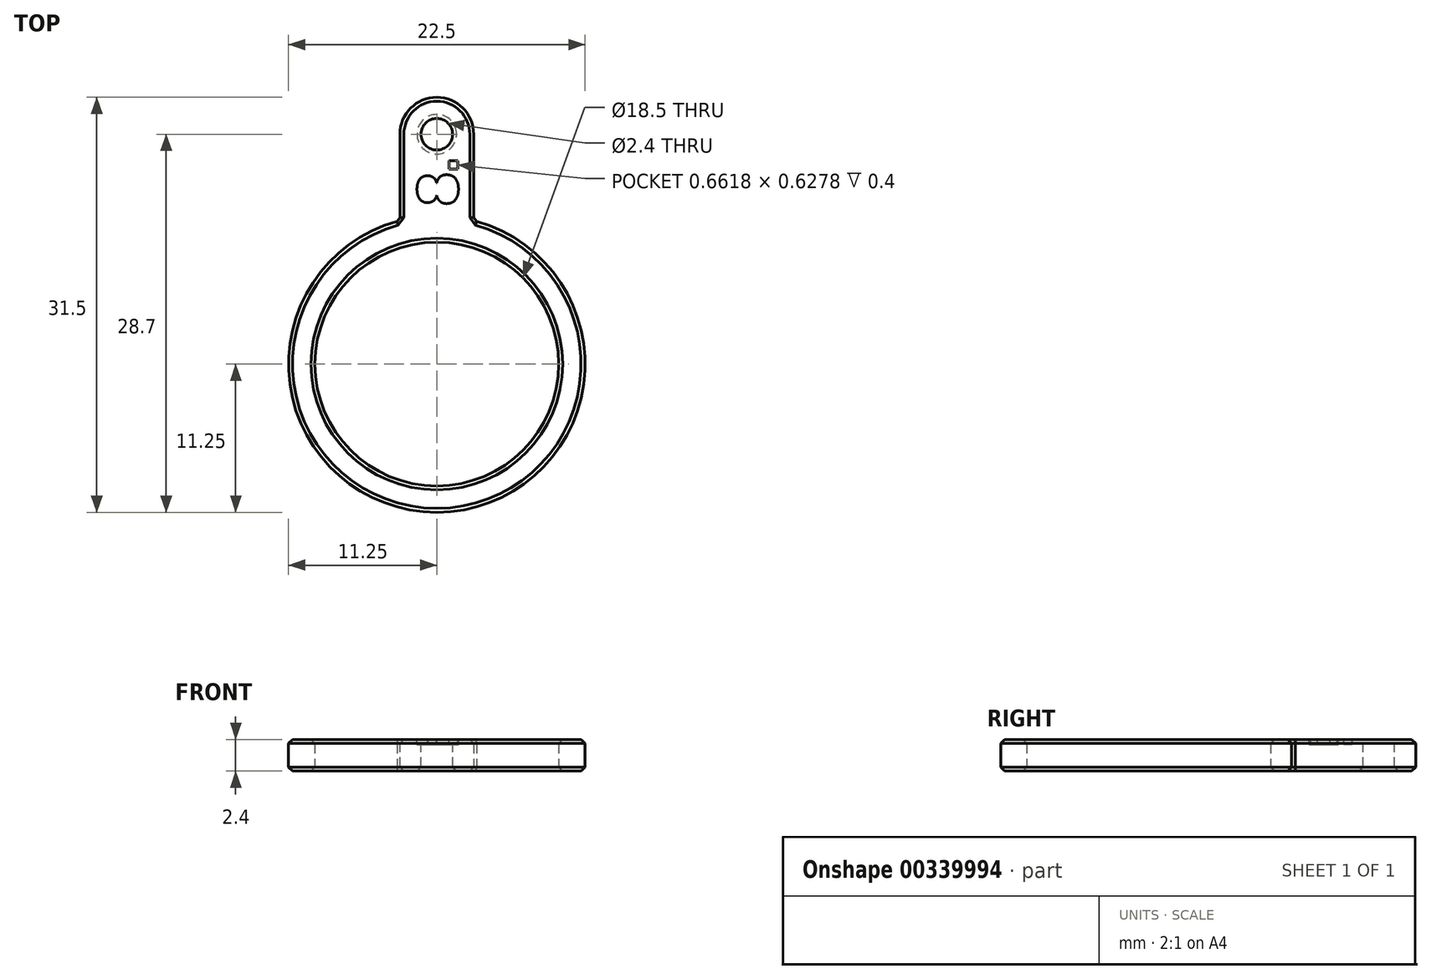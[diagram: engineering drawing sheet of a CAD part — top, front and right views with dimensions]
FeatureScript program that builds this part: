
annotation { "Feature Type Name" : "Feature", "Feature Type Description" : "" }
export const myFeature = defineFeature(function(context is Context, id is Id, definition is map)
    precondition{}
    {
        {
            var Q0;
            Q0=qCreatedBy(makeId("Top.planeOp"),FACE);
            var sketch = newSketch(context, id + "F0", { "sketchPlane" : qUnion([Q0])});
            skCircle(sketch, "E0", {"center": v(0, 0) * mm, "radius": 9.25 * mm});
            skCircle(sketch, "E1", {"center": v(0, 0) * mm, "radius": 11.25 * mm});
            skLineSegment(sketch, "E2.bottom", {"start": v(2.8, 2.25) * mm, "end": v(-2.8, 2.25) * mm});
            skLineSegment(sketch, "E2.top", {"start": v(2.8, 20.25) * mm, "end": v(-2.8, 20.25) * mm});
            skLineSegment(sketch, "E2.left", {"start": v(2.8, 2.25) * mm, "end": v(2.8, 20.25) * mm});
            skLineSegment(sketch, "E2.right", {"start": v(-2.8, 2.25) * mm, "end": v(-2.8, 20.25) * mm});
            skPoint(sketch, "E2.middle", {"position": v(0, 11.25) * mm});
            skSolve(sketch);
        }
        {
            var Q0;
            Q0=qSketchRegion(id+"F0",true);
            extrude(context, id + "F1", {"entities" : qUnion([Q0]), "depth" : 2.4 * mm});
        }
        {
            var Q0;
            Q0=makeQuery(id+"F1.opExtrude","SWEPT_EDGE",EDGE,{"disambiguationData":[OSD([sQuery(id+"F0.wireOp",EDGE,"E2.top"),sQuery(id+"F0.wireOp",EDGE,"E2.right")])]});
            var Q1;
            Q1=makeQuery(id+"F1.opExtrude","SWEPT_EDGE",EDGE,{"disambiguationData":[OSD([sQuery(id+"F0.wireOp",EDGE,"E2.top"),sQuery(id+"F0.wireOp",EDGE,"E2.left")])]});
            fillet(context, id + "F2", {"entities" : qUnion([Q0, Q1]), "radius" : 2.8 * mm, "tangentPropagation" : true, "allowEdgeOverflow" : false});
        }
        {
            var Q0;
            Q0=makeQuery(id+"F1.opExtrude","CAP_FACE",FACE,{"disambiguationData":[OSD([sQuery(id+"F0.wireOp",EDGE,"E0"),sQuery(id+"F0.wireOp",EDGE,"E1"),sQuery(id+"F0.wireOp",EDGE,"E2.top"),sQuery(id+"F0.wireOp",EDGE,"E2.left"),sQuery(id+"F0.wireOp",EDGE,"E2.right")])],"isStart":false});
            var sketch = newSketch(context, id + "F3", { "sketchPlane" : qUnion([Q0])});
            skCircle(sketch, "E3", {"center": v(0, 17.45) * mm, "radius": 1.2 * mm});
            skSolve(sketch);
        }
        {
            var Q0;
            Q0=qSketchRegion(id+"F3",true);
            extrude(context, id + "F4", {"entities" : qUnion([Q0]), "operationType" : NewBodyOperationType.REMOVE, "oppositeDirection" : true, "depth" : 25 * mm});
        }
        {
            var Q0;
            Q0=makeQuery(id+"F4.boolean.opBoolean","COPY",EDGE,{"derivedFrom":makeQuery(id+"F4.opExtrude","CAP_EDGE",EDGE,{"disambiguationData":[OSD([sQuery(id+"F3.wireOp",EDGE,"E3")])],"isStart":true})});
            var Q1;
            Q1=makeQuery(id+"F4.boolean.opBoolean","INTERSECT",EDGE,{"derivedFrom":[makeQuery(id+"F1.opExtrude","CAP_FACE",FACE,{"disambiguationData":[OSD([sQuery(id+"F0.wireOp",EDGE,"E0"),sQuery(id+"F0.wireOp",EDGE,"E1"),sQuery(id+"F0.wireOp",EDGE,"E2.top"),sQuery(id+"F0.wireOp",EDGE,"E2.left"),sQuery(id+"F0.wireOp",EDGE,"E2.right")])],"isStart":true}),makeQuery(id+"F4.opExtrude","SWEPT_FACE",FACE,{"disambiguationData":[OSD([sQuery(id+"F3.wireOp",EDGE,"E3")])]})]});
            var Q2;
            {var subQ0=sQuery(id+"F0.wireOp",EDGE,"E2.right");var subQ1=sQuery(id+"F0.wireOp",EDGE,"E2.top");Q2=makeQuery(id+"F2.opFillet","BLEND_EDGE",EDGE,{"blendedFrom":[makeQuery(id+"F1.opExtrude","SWEPT_EDGE",EDGE,{"disambiguationData":[OSD([subQ1,subQ0])]}),makeQuery(id+"F1.opExtrude","CAP_FACE",FACE,{"disambiguationData":[OSD([sQuery(id+"F0.wireOp",EDGE,"E0"),sQuery(id+"F0.wireOp",EDGE,"E1"),subQ1,sQuery(id+"F0.wireOp",EDGE,"E2.left"),subQ0])],"isStart":true})],"blendedInto":[makeQuery(id+"F1.opExtrude","CAP_FACE",FACE,{"disambiguationData":[OSD([sQuery(id+"F0.wireOp",EDGE,"E0"),sQuery(id+"F0.wireOp",EDGE,"E1"),subQ1,sQuery(id+"F0.wireOp",EDGE,"E2.left"),subQ0])],"isStart":true})]});}
            var Q3;
            {var subQ0=sQuery(id+"F0.wireOp",EDGE,"E2.right");var subQ1=sQuery(id+"F0.wireOp",EDGE,"E2.top");Q3=makeQuery(id+"F2.opFillet","BLEND_EDGE",EDGE,{"blendedFrom":[makeQuery(id+"F1.opExtrude","SWEPT_EDGE",EDGE,{"disambiguationData":[OSD([subQ1,subQ0])]}),makeQuery(id+"F1.opExtrude","CAP_FACE",FACE,{"disambiguationData":[OSD([sQuery(id+"F0.wireOp",EDGE,"E0"),sQuery(id+"F0.wireOp",EDGE,"E1"),subQ1,sQuery(id+"F0.wireOp",EDGE,"E2.left"),subQ0])],"isStart":false})],"blendedInto":[makeQuery(id+"F1.opExtrude","CAP_FACE",FACE,{"disambiguationData":[OSD([sQuery(id+"F0.wireOp",EDGE,"E0"),sQuery(id+"F0.wireOp",EDGE,"E1"),subQ1,sQuery(id+"F0.wireOp",EDGE,"E2.left"),subQ0])],"isStart":false})]});}
            var Q4;
            Q4=makeQuery(id+"F1.opExtrude","CAP_EDGE",EDGE,{"disambiguationData":[OSD([sQuery(id+"F0.wireOp",EDGE,"E1")])],"isStart":false});
            var Q5;
            Q5=makeQuery(id+"F1.opExtrude","CAP_EDGE",EDGE,{"disambiguationData":[OSD([sQuery(id+"F0.wireOp",EDGE,"E1")])],"isStart":true});
            var Q6;
            Q6=makeQuery(id+"F1.opExtrude","SWEPT_EDGE",EDGE,{"disambiguationData":[OSD([sQuery(id+"F0.wireOp",EDGE,"E1"),sQuery(id+"F0.wireOp",EDGE,"E2.left")])]});
            var Q7;
            Q7=makeQuery(id+"F1.opExtrude","SWEPT_EDGE",EDGE,{"disambiguationData":[OSD([sQuery(id+"F0.wireOp",EDGE,"E1"),sQuery(id+"F0.wireOp",EDGE,"E2.right")])]});
            var Q8;
            Q8=makeQuery(id+"F1.opExtrude","CAP_EDGE",EDGE,{"disambiguationData":[OSD([sQuery(id+"F0.wireOp",EDGE,"E0")])],"isStart":true});
            var Q9;
            Q9=makeQuery(id+"F1.opExtrude","CAP_EDGE",EDGE,{"disambiguationData":[OSD([sQuery(id+"F0.wireOp",EDGE,"E0")])],"isStart":false});
            chamfer(context, id + "F5", {"entities" : qUnion([Q0, Q1, Q2, Q3, Q4, Q5, Q6, Q7, Q8, Q9]), "width" : 0.3 * mm, "tangentPropagation" : true});
        }
        {
            var Q0;
            Q0=makeQuery(id+"F1.opExtrude","CAP_FACE",FACE,{"disambiguationData":[OSD([sQuery(id+"F0.wireOp",EDGE,"E0"),sQuery(id+"F0.wireOp",EDGE,"E1"),sQuery(id+"F0.wireOp",EDGE,"E2.top"),sQuery(id+"F0.wireOp",EDGE,"E2.left"),sQuery(id+"F0.wireOp",EDGE,"E2.right")])],"isStart":false});
            var sketch = newSketch(context, id + "F6", { "sketchPlane" : qUnion([Q0])});
            skText(sketch, "E4", { "text": "8.", "fontName": "Arimo-Bold.ttf"});
            skLineSegment(sketch, "E5", {"start": v(0, 12.24) * mm, "end": v(0, 0) * mm});
            skPoint(sketch, "E5.endSnap0", {"position": v(0, 12.24) * mm});
            const initialGuessF6  = {"E4": [0.0016, 0.01204, 0, 1, 0.0032]};
            skSetInitialGuess(sketch, initialGuessF6);
            skSolve(sketch);
        }
        {
            var Q0;
            Q0=qSketchRegion(id+"F6",true);
            var Q1;
            Q1=makeQuery(id+"F6.imprint","IMPRINT",FACE,{"disambiguationData":[TD([[makeQuery(id+"F6.imprint","IMPRINT",EDGE,{"derivedFrom":sQuery(id+"F6.wireOp",EDGE,"E4.sketch_text.stroke-18")}),1.0]])]});
            var Q2;
            Q2=makeQuery(id+"F6.imprint","IMPRINT",FACE,{"disambiguationData":[TD([[makeQuery(id+"F6.imprint","IMPRINT",EDGE,{"derivedFrom":sQuery(id+"F6.wireOp",EDGE,"E4.sketch_text.stroke-24")}),1.0]])]});
            extrude(context, id + "F7", {"entities" : qUnion([Q0, Q1, Q2]), "operationType" : NewBodyOperationType.REMOVE, "oppositeDirection" : true, "depth" : 0.4 * mm});
        }
    });
